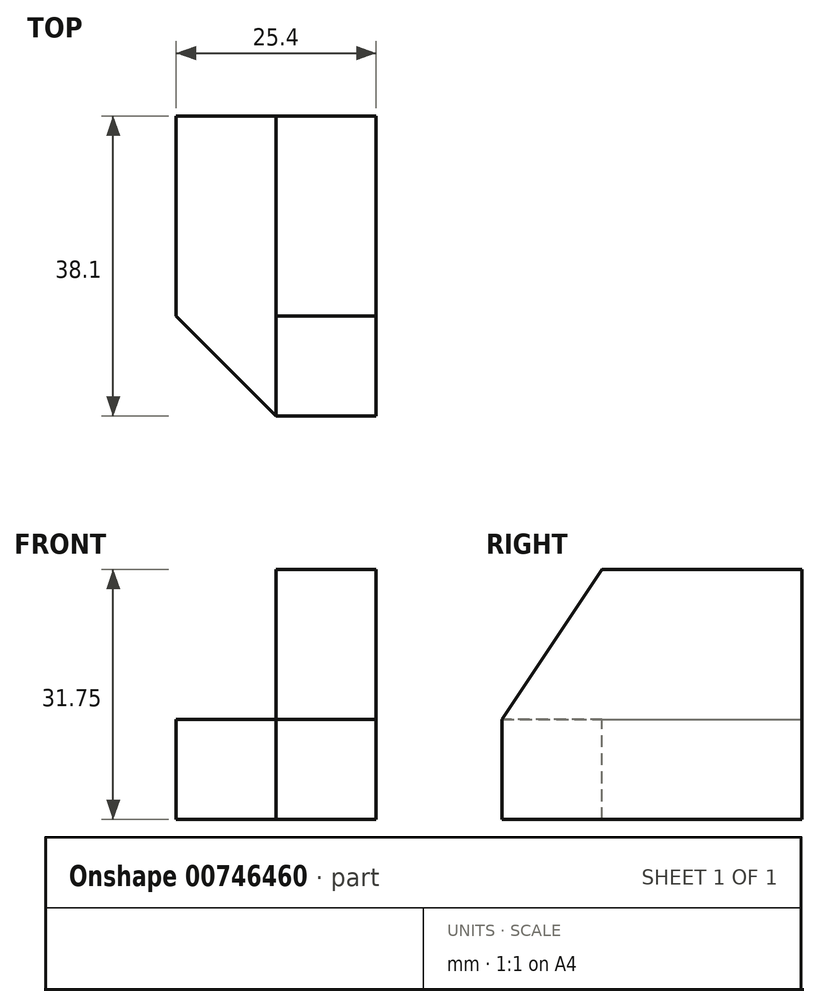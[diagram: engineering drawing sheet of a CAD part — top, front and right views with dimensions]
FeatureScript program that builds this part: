
annotation { "Feature Type Name" : "Feature", "Feature Type Description" : "" }
export const myFeature = defineFeature(function(context is Context, id is Id, definition is map)
    precondition{}
    {
        {
            var Q0;
            Q0=qCreatedBy(makeId("Front.planeOp"),FACE);
            var sketch = newSketch(context, id + "F0", { "sketchPlane" : qUnion([Q0])});
            skLineSegment(sketch, "E0", {"start": v(0, 0) * mm, "end": v(25.4, 0) * mm});
            skLineSegment(sketch, "E1", {"start": v(25.4, 0) * mm, "end": v(25.4, 31.75) * mm});
            skLineSegment(sketch, "E2", {"start": v(25.4, 31.75) * mm, "end": v(12.7, 31.75) * mm});
            skLineSegment(sketch, "E3", {"start": v(12.7, 31.75) * mm, "end": v(12.7, 12.7) * mm});
            skLineSegment(sketch, "E4", {"start": v(12.7, 12.7) * mm, "end": v(0, 12.7) * mm});
            skLineSegment(sketch, "E5", {"start": v(0, 12.7) * mm, "end": v(0, 0) * mm});
            skSolve(sketch);
        }
        {
            var Q0;
            Q0=makeQuery(id+"F0.imprint","IMPRINT",FACE,{"disambiguationData":[TD([[makeQuery(id+"F0.imprint","IMPRINT",EDGE,{"derivedFrom":sQuery(id+"F0.wireOp",EDGE,"E0")}),1.0]])]});
            extrude(context, id + "F1", {"entities" : qUnion([Q0]), "depth" : 38.1 * mm, "offsetDistance" : 25.4 * mm});
        }
        {
            var Q0;
            Q0=makeQuery(id+"F1.opExtrude","SWEPT_FACE",FACE,{"disambiguationData":[OSD([sQuery(id+"F0.wireOp",EDGE,"E3")])]});
            var sketch = newSketch(context, id + "F2", { "sketchPlane" : qUnion([Q0])});
            skLineSegment(sketch, "E6", {"start": v(0, 31.75) * mm, "end": v(0, 53.77) * mm});
            skLineSegment(sketch, "E7", {"start": v(0, 53.77) * mm, "end": v(25.4, 53.77) * mm});
            skLineSegment(sketch, "E8", {"start": v(25.4, 53.77) * mm, "end": v(25.4, 31.75) * mm});
            skLineSegment(sketch, "E9", {"start": v(25.4, 31.75) * mm, "end": v(0, 31.75) * mm});
            skLineSegment(sketch, "E10", {"start": v(25.4, 31.75) * mm, "end": v(38.1, 12.7) * mm});
            skSolve(sketch);
        }
        {
            var Q0;
            Q0 = qSketchRegion(id + "F2", true);
            var Q1;
            {var subQ0=sQuery(id+"F2.wireOp",EDGE,"E10");Q1=makeQuery(id+"F2.imprint","IMPRINT",FACE,{"disambiguationData":[TD([[makeQuery(id+"F2.imprint","IMPRINT",EDGE,{"derivedFrom":subQ0}),1.0]])]});}
            extrude(context, id + "F3", {"entities" : qUnion([Q0, Q1]), "operationType" : NewBodyOperationType.REMOVE, "oppositeDirection" : true, "depth" : 12.7 * mm, "offsetDistance" : 25.4 * mm});
        }
        {
            var Q0;
            Q0=makeQuery(id+"F1.opExtrude","SWEPT_FACE",FACE,{"disambiguationData":[OSD([sQuery(id+"F0.wireOp",EDGE,"E4")])]});
            var sketch = newSketch(context, id + "F4", { "sketchPlane" : qUnion([Q0])});
            skLineSegment(sketch, "E11", {"start": v(0, -38.1) * mm, "end": v(12.7, -38.1) * mm});
            skLineSegment(sketch, "E12", {"start": v(0, -38.1) * mm, "end": v(0, -25.4) * mm});
            skLineSegment(sketch, "E13", {"start": v(0, -25.4) * mm, "end": v(12.7, -38.1) * mm});
            skSolve(sketch);
        }
        {
            var Q0;
            Q0=makeQuery(id+"F4.imprint","IMPRINT",FACE,{"disambiguationData":[TD([[makeQuery(id+"F4.imprint","IMPRINT",EDGE,{"derivedFrom":sQuery(id+"F4.wireOp",EDGE,"E11")}),-1.0]])]});
            extrude(context, id + "F5", {"entities" : qUnion([Q0]), "operationType" : NewBodyOperationType.REMOVE, "oppositeDirection" : true, "depth" : 12.7 * mm, "offsetDistance" : 25.4 * mm});
        }
    });
